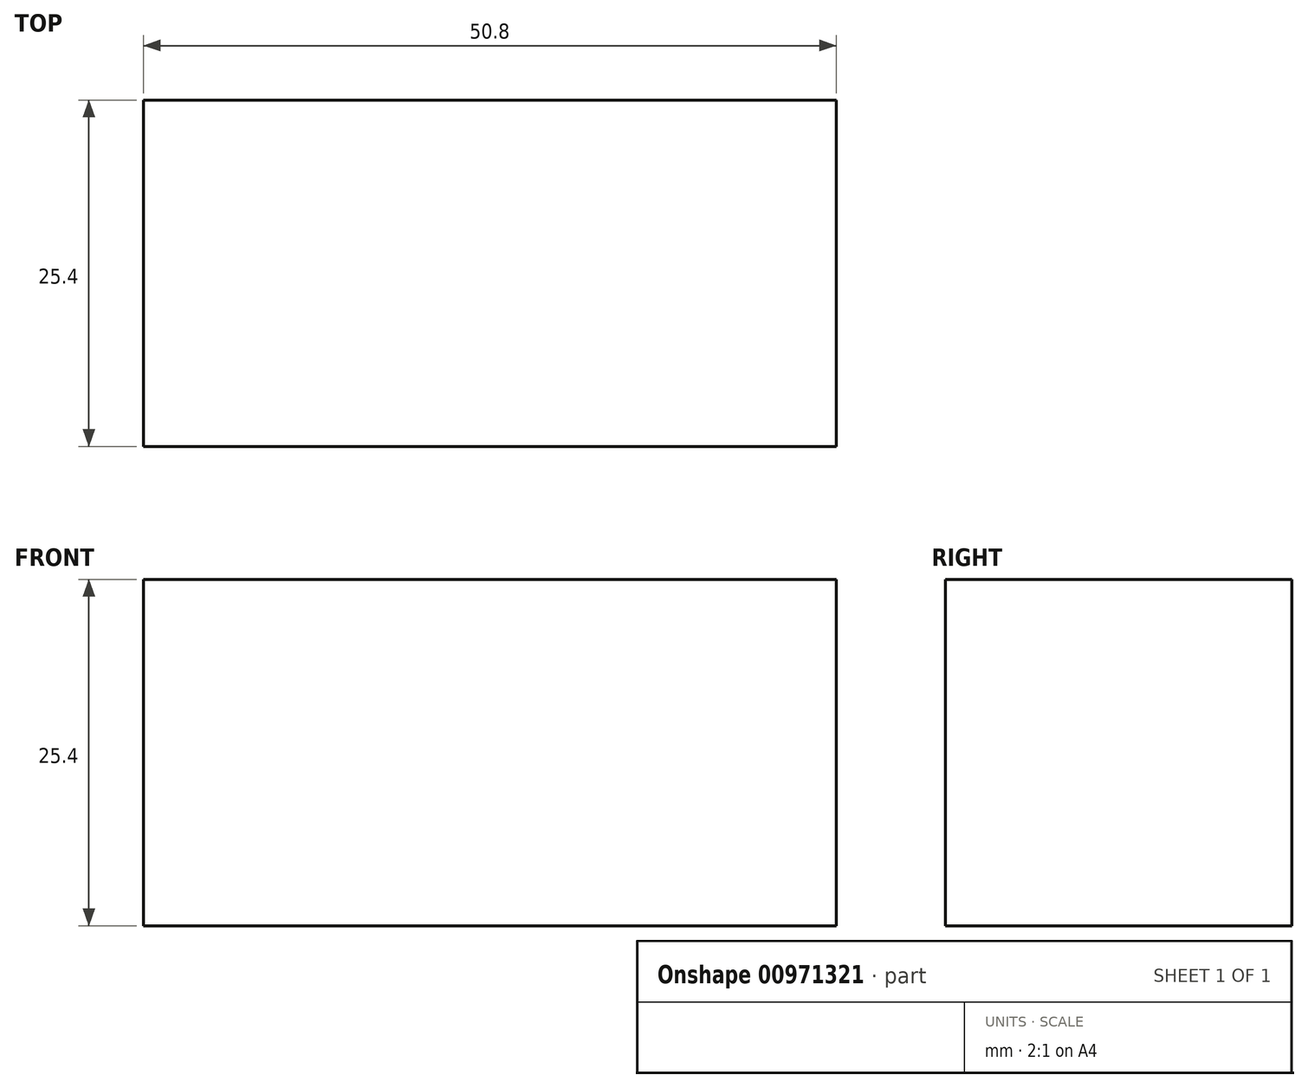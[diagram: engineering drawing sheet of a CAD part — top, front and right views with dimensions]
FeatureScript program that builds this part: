
annotation { "Feature Type Name" : "Feature", "Feature Type Description" : "" }
export const myFeature = defineFeature(function(context is Context, id is Id, definition is map)
    precondition{}
    {
        {
            var Q0;
            Q0=qCreatedBy(makeId("Top.planeOp"),FACE);
            var sketch = newSketch(context, id + "F0", { "sketchPlane" : qUnion([Q0])});
            skLineSegment(sketch, "E0.bottom", {"start": v(0, 0) * mm, "end": v(50.8, 0) * mm});
            skLineSegment(sketch, "E0.top", {"start": v(0, 25.4) * mm, "end": v(50.8, 25.4) * mm});
            skLineSegment(sketch, "E0.left", {"start": v(0, 0) * mm, "end": v(0, 25.4) * mm});
            skLineSegment(sketch, "E0.right", {"start": v(50.8, 0) * mm, "end": v(50.8, 25.4) * mm});
            skSolve(sketch);
        }
        {
            var Q0;
            Q0 = qSketchRegion(id + "F0", true);
            extrude(context, id + "F1", {"entities" : qUnion([Q0]), "depth" : 25.4 * mm, "offsetDistance" : 25.4 * mm});
        }
    });
